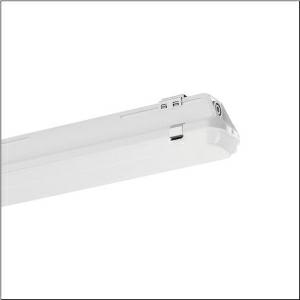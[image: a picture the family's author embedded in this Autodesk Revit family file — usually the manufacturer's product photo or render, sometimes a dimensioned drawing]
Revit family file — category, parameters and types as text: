
# Revit family: monsun_r__21_51fb10mp480b_b142
name_source: partatom
category: Lighting Fixtures
units: mm (PartAtom-declared; Revit-internal decimal feet)

## family parameters
Cut with Voids When Loaded = No
Host = Face
Light Source = No
Part Type = Normal
Room Calculation Point = No
Round Connector Dimension = Use Diameter
Shared = No

## types (1)
- --- (1 x LED, 8190 lm, 53.6 W, 4000K)
    Apparent Load = 54 VA
    CIE Flux Codes = 47 77 93 94 100
    Color Rendering = 80
    Color Temperature = 4000K
    Default Elevation = 1800 mm
    Description = Monsun® 21, damp-proof luminaire, chain hanger, primary optical cover: enclosure, of PMMA, light emission: direct distribution, primary light characteristic: symmetric, installation type: suspended mounting, surface-mounted, horizontal mounting, vertical mounting, LED, rated luminous flux: 8.190lm, luminous efficacy: 153lm/W, light colour: 840, colour temperature: 4000K, control gear: ECG, with terminal, 3-pole, max. 2.5mm², mains connection: 220..240V, AC, 50/60Hz, rated input power: 54W, housing, of glass-fibre reinforced polyester, uncoated, bright grey, length: 1.590mm, width: 90mm, height: 88mm, clip for enclosure, of stainless steel (V2A), ceiling mounting element, of stainless steel (V2A), chain hanger, of stainless steel (V2A), protection rating (complete): IP66, insulation class (complete): insulation class I (protective earthing), certification: CE, ENEC, VDE, UKCA, protection symbol: D, impact resistance: IK04, permissible operating ambient temperature: -25..+35°C, standard: EN 50419, EN 60598-2-1, corresponds to IFS (International Featured Standards) requirements for safety and quality in the food industry, for indoor or canopied outdoor use, no direct snow, no direct sun, no direct rain, packaging unit: 1 piece
    Height = 89 mm
    Lamp = 1 x LED
    Lamp Light Flux = 8190 lm
    Lamp Power = 53.6 W
    Lamp count = 1
    Length = 1590 mm
    Luminous efficacy = 153 lm/W
    Manufacturer = Siteco
    ModVariant = No
    Model = 51FB10MP480B
    Mounting Place = Ceiling
    Mounting Type = Pendant
    Number of Poles = 1
    OnlyDefault = Yes
    Power Factor = 1
    Product Name = Monsun® 21
    Product group = damp-proof luminaire | ceiling pendant
    ProductGroupID = 908
    Protection Class = Protection class I
    Protection Degree = IP 66
    RLX_Detail_Level = 1
    RlxData = <blob elided: 89685 chars, md5=0ae099c6>
    Socket = socket
    Standby Power = 0 W
    System Light Flux = 8190 lm
    System Power = 54 W
    Type Comments = factory setting: luminous flux: 100 % | (A | C | E) | 121 mA
    Type Image = l_1006717.jpg
    URL = http://relux.com
    VarID = @adj_056915
    Voltage = 0 V
    Weight = 0.00 kg
    Width = 90 mm

## geometry (parser evidence)
native form markers: Blend x4, Sweep x13
no freeform markers — native parametric forms only
